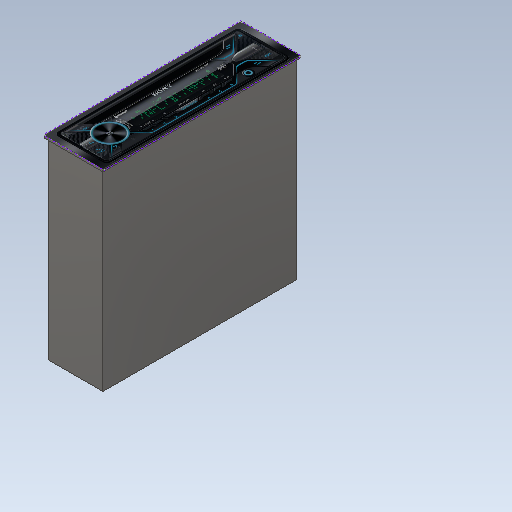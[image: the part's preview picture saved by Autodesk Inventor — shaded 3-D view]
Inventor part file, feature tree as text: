
AUTODESK INVENTOR PART (.ipt)
format: ipt  version: 2021 (Build 250183000, 183)  size: 564,224 bytes
history: native  units: mm
features: sketch x3, extrude x2, other x1
ambient origin geometry x8: Origin, YZ Plane, XZ Plane, XY Plane, X Axis, Y Axis, Z Axis, Center Point
bodies: Solid1 (feature_tree)
feature tree (6):
  extrude  "Extrusion1"  Depth=50.0mm
  extrude  "Extrusion2"  TaperAngle=0.0deg  [1 undecoded]
  sketch  "Sketch3"  dims[d4=2.0mm d5=2.0mm d6=2.0mm d7=0.0mm]
  sketch  "Sketch1"  dims[d0=178.0mm d1=50.0mm]
  sketch  "Sketch2"  dims[d2=177.0mm d3=0.0mm]
  other  "Image1"
note: 1 required parameter value undecoded (feature->parameter linkage not recoverable at this tier; creation-order binding heuristic only, values carry confidence <= 0.55)
